# Revit family: Shower-Slidebar-KOHLER-WATER_SUPPLY-K-2738T-1
name_source: partatom
category: Plumbing Fixtures
units: mm (PartAtom-declared; Revit-internal decimal feet)

## family parameters
Cut with Voids When Loaded = No
Host = Face
OmniClass Number = 23.31.25.00
OmniClass Title = Toilet and Bath Specialties
Part Type = Normal
Room Calculation Point = No
Round Connector Dimension = Use Diameter
Shared = No

## types (5) — shared parameters
ADA Compliant = No
Assembly Code = D2010700
CW Connection = No
Cold Water Inlet = Cold Water Inlet
Date Modified = 05/18/2024
Default Elevation = 42"
Description = Sliding shower bracket (water supply)
Drain Included = No
Flow Rate = 0 GPM
HW Connection = Yes
Height = 30 9/16"
Hot Water Inlet = Hot Water Inlet
Length = 3 1/8"
Manufacturer = Kohler Co.
Master Format 2014 = 22 42 23
Master Format 2014 Name = Residential Showers
Material = Premium Metal Construction
Pressure = 0.00 psi
Product Documentation Link = https://files.kohler.com.cn
Product Name = WATER SUPPLY
Tempered Water Inlet = Tempered Water Inlet
URL = http://www.kohler.com.cn
Vent Connection = No
Waste Connection = No
Waste Water Outlet = Waste Water Outlet
WaterSense Certified = No
Width = 3 5/16"

## per-type parameters (varying)
| type | Finish | Model | Product Page URL | Type |
| CP-Polished Chrome | Kohler-Metal-CP-Polished_Chrome | K-2738T-CP | https://www.kohler.com.cn | 1 |
| BRD-Brushed Rose Gold | KOHLER-Metal-BRD-Brushed_Rose_Gold | K-2738T-BRD |  | 2 |
| BRT-Brushed Titanium | KOHLER-Metal-BRT-Brushed_Titanium | K-2738T-BRT |  | 3 |
| BGP | Kohler-Metal-BGP | K-2738T-BGP |  | 4 |
| PGP | Kohler-Metal-PGP | K-2738T-PGP |  | 5 |

## geometry (parser evidence)
native form markers: Sweep x5
no freeform markers — native parametric forms only
